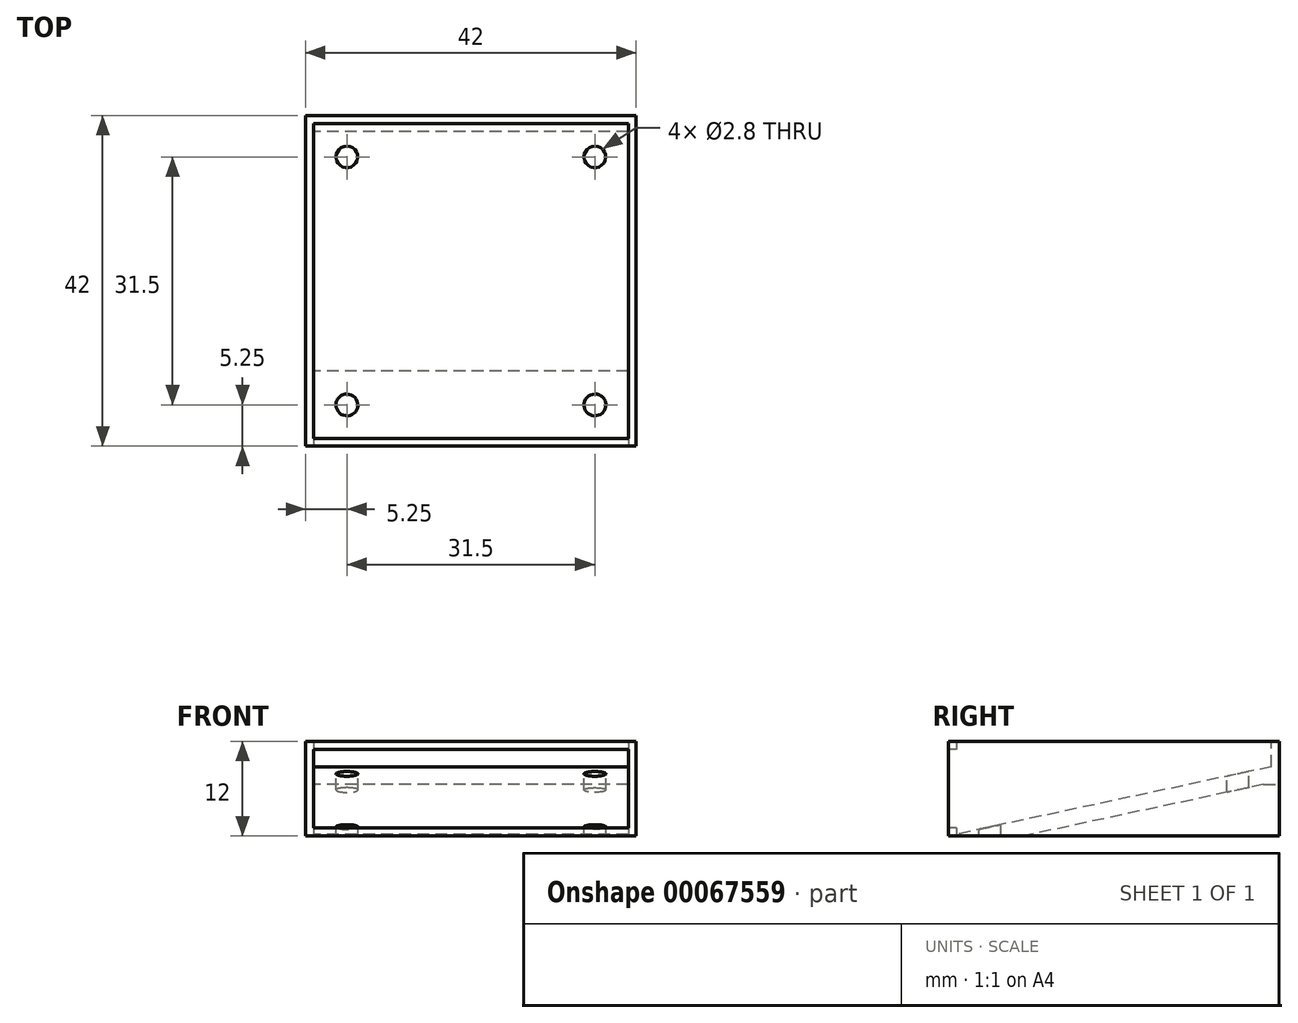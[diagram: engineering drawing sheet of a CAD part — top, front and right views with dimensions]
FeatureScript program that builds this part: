
annotation { "Feature Type Name" : "Feature", "Feature Type Description" : "" }
export const myFeature = defineFeature(function(context is Context, id is Id, definition is map)
    precondition{}
    {
        {
            var Q0;
            Q0=qCreatedBy(makeId("Top.planeOp"),FACE);
            var sketch = newSketch(context, id + "F0", { "sketchPlane" : qUnion([Q0])});
            skLineSegment(sketch, "E0.rect.bottom", {"start": v(21, -21) * mm, "end": v(-21, -21) * mm});
            skLineSegment(sketch, "E0.rect.top", {"start": v(21, 21) * mm, "end": v(-21, 21) * mm});
            skLineSegment(sketch, "E0.rect.left", {"start": v(21, -21) * mm, "end": v(21, 21) * mm});
            skLineSegment(sketch, "E0.rect.right", {"start": v(-21, -21) * mm, "end": v(-21, 21) * mm});
            skPoint(sketch, "E0.rect.middle", {"position": v(0, 0) * mm});
            skLineSegment(sketch, "E1.rect.bottom", {"start": v(15.75, -15.75) * mm, "end": v(-15.75, -15.75) * mm, "construction": true});
            skLineSegment(sketch, "E1.rect.top", {"start": v(15.75, 15.75) * mm, "end": v(-15.75, 15.75) * mm, "construction": true});
            skLineSegment(sketch, "E1.rect.left", {"start": v(15.75, -15.75) * mm, "end": v(15.75, 15.75) * mm, "construction": true});
            skLineSegment(sketch, "E1.rect.right", {"start": v(-15.75, -15.75) * mm, "end": v(-15.75, 15.75) * mm, "construction": true});
            skLineSegment(sketch, "E2", {"start": v(0, 21) * mm, "end": v(0, -21) * mm});
            skSolve(sketch);
        }
        {
            var Q0;
            {var subQ0=sQuery(id+"F0.wireOp",EDGE,"E0.rect.left");Q0=makeQuery(id+"F0.imprint","IMPRINT",FACE,{"disambiguationData":[TD([[makeQuery(id+"F0.imprint","IMPRINT",EDGE,{"derivedFrom":subQ0}),1.0]])]});}
            extrude(context, id + "F1", {"entities" : qUnion([Q0]), "oppositeDirection" : true, "depth" : 12 * mm});
        }
        {
            var Q0;
            Q0=sQuery(id+"F0.wireOp",VERTEX,"E1.rect.left.end");
            var Q1;
            Q1=sQuery(id+"F0.wireOp",VERTEX,"E1.rect.left.start");
            var Q2;
            Q2=makeQuery(id+"F1.opExtrude","SWEPT_BODY",BODY,{"disambiguationData":[OSD([sQuery(id+"F0.wireOp",EDGE,"E0.rect.bottom"),sQuery(id+"F0.wireOp",EDGE,"E0.rect.top"),sQuery(id+"F0.wireOp",EDGE,"E0.rect.left"),sQuery(id+"F0.wireOp",EDGE,"E2")])]});
            hole(context, id + "F2", {"style" : HoleStyle.SIMPLE, "holeDiameter" : 2.8 * mm, "endStyle" : HoleEndStyle.THROUGH, "locations" : qUnion([Q0, Q1]), "scope" : qUnion([Q2])});
        }
        {
            var Q0;
            Q0=makeQuery(id+"F1.opExtrude","SWEPT_FACE",FACE,{"disambiguationData":[OSD([sQuery(id+"F0.wireOp",EDGE,"E2")])]});
            var sketch = newSketch(context, id + "F3", { "sketchPlane" : qUnion([Q0])});
            skLineSegment(sketch, "E3", {"start": v(-21, -3) * mm, "end": v(21, -12) * mm});
            skPoint(sketch, "E4.0", {"position": v(-15.75, 0) * mm});
            skLineSegment(sketch, "E5", {"start": v(-19, -12) * mm, "end": v(-19, -5.47) * mm});
            skLineSegment(sketch, "E6", {"start": v(-19, -5.47) * mm, "end": v(11.45, -12) * mm});
            skLineSegment(sketch, "E7", {"start": v(20, 0) * mm, "end": v(20, -11.79) * mm});
            skLineSegment(sketch, "E8", {"start": v(-19, -5.47) * mm, "end": v(-21, -5.47) * mm});
            skLineSegment(sketch, "E9", {"start": v(-20, -3.21) * mm, "end": v(-20, 0) * mm});
            skSolve(sketch);
        }
        {
            var Q0;
            {var subQ4=sQuery(id+"F3.wireOp",EDGE,"E7");Q0=makeQuery(id+"F3.imprint","IMPRINT",FACE,{"disambiguationData":[TD([[makeQuery(id+"F3.imprint","IMPRINT",EDGE,{"derivedFrom":subQ4}),-1.0]])]});}
            var Q1;
            {var subQ0=sQuery(id+"F3.wireOp",EDGE,"E5");Q1=makeQuery(id+"F3.imprint","IMPRINT",FACE,{"disambiguationData":[TD([[makeQuery(id+"F3.imprint","IMPRINT",EDGE,{"derivedFrom":subQ0}),-1.0]])]});}
            var Q2;
            {var subQ0=sQuery(id+"F3.wireOp",EDGE,"E5");Q2=makeQuery(id+"F3.imprint","IMPRINT",FACE,{"disambiguationData":[TD([[makeQuery(id+"F3.imprint","IMPRINT",EDGE,{"derivedFrom":subQ0}),1.0]])]});}
            extrude(context, id + "F4", {"entities" : qUnion([Q0, Q1, Q2]), "operationType" : NewBodyOperationType.REMOVE, "oppositeDirection" : true, "depth" : 20 * mm});
        }
        {
            var Q0;
            Q0=makeQuery(id+"F1.opExtrude","SWEPT_BODY",BODY,{"disambiguationData":[OSD([sQuery(id+"F0.wireOp",EDGE,"E0.rect.bottom"),sQuery(id+"F0.wireOp",EDGE,"E0.rect.top"),sQuery(id+"F0.wireOp",EDGE,"E0.rect.left"),sQuery(id+"F0.wireOp",EDGE,"E2")])]});
            var Q1;
            Q1=makeQuery(id+"F1.opExtrude","SWEPT_FACE",FACE,{"disambiguationData":[OSD([sQuery(id+"F0.wireOp",EDGE,"E2")])]});
            mirror(context, id + "F5", {"operationType" : NewBodyOperationType.ADD, "entities" : qUnion([Q0]), "mirrorPlane" : qUnion([Q1])});
        }
        {
            var Q0;
            {var subQ0=makeQuery(id+"F1.opExtrude","SWEPT_FACE",FACE,{"disambiguationData":[OSD([sQuery(id+"F0.wireOp",EDGE,"E0.rect.bottom")])]});Q0=makeQuery(id+"F5.boolean.opBoolean","MERGE",FACE,{"derivedFrom":[subQ0,makeQuery(id+"F5.opPattern","COPY",FACE,{"derivedFrom":subQ0,"instanceName":"1"})]});}
            var sketch = newSketch(context, id + "F6", { "sketchPlane" : qUnion([Q0])});
            skLineSegment(sketch, "E10.0", {"start": v(20, -1) * mm, "end": v(-20, -1) * mm});
            skLineSegment(sketch, "E10.1", {"start": v(20, -11) * mm, "end": v(20, -1) * mm});
            skLineSegment(sketch, "E10.2", {"start": v(-20, -11) * mm, "end": v(20, -11) * mm});
            skLineSegment(sketch, "E10.3", {"start": v(-20, -1) * mm, "end": v(-20, -11) * mm});
            skLineSegment(sketch, "E11.0", {"start": v(26, 5) * mm, "end": v(-26, 5) * mm});
            skLineSegment(sketch, "E11.1", {"start": v(26, -17) * mm, "end": v(26, 5) * mm});
            skLineSegment(sketch, "E11.2", {"start": v(-26, -17) * mm, "end": v(26, -17) * mm});
            skLineSegment(sketch, "E11.3", {"start": v(-26, 5) * mm, "end": v(-26, -17) * mm});
            skSolve(sketch);
        }
        {
            var Q0;
            Q0=makeQuery(id+"F6.imprint","IMPRINT",FACE,{"disambiguationData":[TD([[makeQuery(id+"F6.imprint","IMPRINT",EDGE,{"derivedFrom":sQuery(id+"F6.wireOp",EDGE,"E10.0")}),1.0]])]});
            extrude(context, id + "F7", {"entities" : qUnion([Q0]), "operationType" : NewBodyOperationType.REMOVE, "oppositeDirection" : true, "depth" : 1 * mm});
        }
    });
